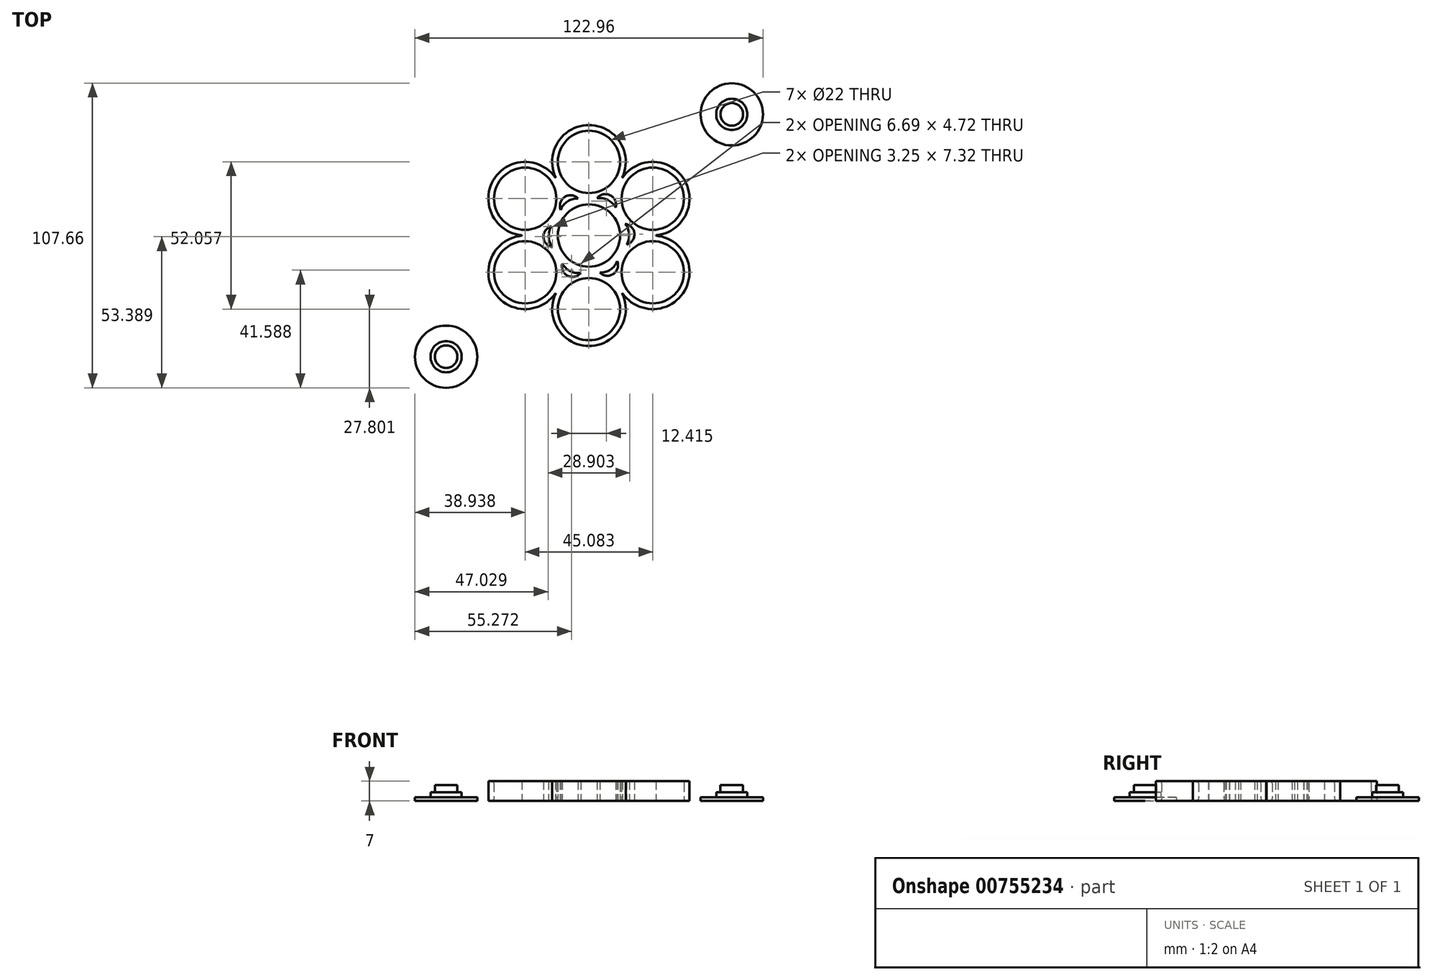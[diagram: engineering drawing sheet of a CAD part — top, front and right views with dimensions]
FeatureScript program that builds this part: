
annotation { "Feature Type Name" : "Feature", "Feature Type Description" : "" }
export const myFeature = defineFeature(function(context is Context, id is Id, definition is map)
    precondition{}
    {
        {
            var Q0;
            Q0=qCreatedBy(makeId("Top.planeOp"),FACE);
            var sketch = newSketch(context, id + "F0", { "sketchPlane" : qUnion([Q0])});
            skCircle(sketch, "E0", {"center": v(0, 0) * mm, "radius": 11 * mm});
            skCircle(sketch, "E1", {"center": v(0, 26.03) * mm, "radius": 11 * mm});
            skArc(sketch, "E2", {"start": v(11.75, 20.47) * mm, "mid": v(0, 39.03) * mm, "end": v(-11.76, 20.48) * mm});
            skCircle(sketch, "E3.1.0", {"center": v(-22.54, 13.01) * mm, "radius": 11 * mm});
            skArc(sketch, "E3.1.1", {"start": v(-11.85, 20.41) * mm, "mid": v(-33.8, 19.52) * mm, "end": v(-23.61, 0.06) * mm});
            skCircle(sketch, "E3.2.0", {"center": v(-22.54, -13.01) * mm, "radius": 11 * mm});
            skArc(sketch, "E3.2.1", {"start": v(-23.6, -0.06) * mm, "mid": v(-33.8, -19.51) * mm, "end": v(-11.86, -20.42) * mm});
            skCircle(sketch, "E3.3.0", {"center": v(0, -26.03) * mm, "radius": 11 * mm});
            skArc(sketch, "E3.3.1", {"start": v(-11.75, -20.47) * mm, "mid": v(0, -39.03) * mm, "end": v(11.76, -20.48) * mm});
            skCircle(sketch, "E3.4.0", {"center": v(22.54, -13.01) * mm, "radius": 11 * mm});
            skArc(sketch, "E3.4.1", {"start": v(11.85, -20.41) * mm, "mid": v(33.8, -19.52) * mm, "end": v(23.61, -0.06) * mm});
            skCircle(sketch, "E3.5.0", {"center": v(22.54, 13.01) * mm, "radius": 11 * mm});
            skArc(sketch, "E3.5.1", {"start": v(23.6, 0.06) * mm, "mid": v(33.8, 19.51) * mm, "end": v(11.86, 20.42) * mm});
            skArc(sketch, "E4", {"start": v(11.86, 20.42) * mm, "mid": v(11.85, 20.53) * mm, "end": v(11.75, 20.47) * mm});
            skArc(sketch, "E5.1.0", {"start": v(-11.76, 20.48) * mm, "mid": v(-11.86, 20.52) * mm, "end": v(-11.85, 20.41) * mm});
            skArc(sketch, "E5.2.0", {"start": v(-23.61, 0.06) * mm, "mid": v(-23.7, 0) * mm, "end": v(-23.6, -0.06) * mm});
            skArc(sketch, "E5.3.0", {"start": v(-11.86, -20.42) * mm, "mid": v(-11.85, -20.53) * mm, "end": v(-11.75, -20.47) * mm});
            skArc(sketch, "E5.4.0", {"start": v(11.76, -20.48) * mm, "mid": v(11.86, -20.52) * mm, "end": v(11.85, -20.41) * mm});
            skArc(sketch, "E5.5.0", {"start": v(23.61, -0.06) * mm, "mid": v(23.7, 0) * mm, "end": v(23.6, 0.06) * mm});
            skArc(sketch, "E6", {"start": v(13.27, -3.22) * mm, "mid": v(16.08, 0.62) * mm, "end": v(12.83, 4.1) * mm});
            skArc(sketch, "E7", {"start": v(13.27, -3.22) * mm, "mid": v(14.22, 0.51) * mm, "end": v(12.83, 4.1) * mm});
            skArc(sketch, "E8.1.0", {"start": v(9.42, 9.88) * mm, "mid": v(6.67, 12.57) * mm, "end": v(2.86, 13.16) * mm});
            skArc(sketch, "E8.1.1", {"start": v(9.42, 9.88) * mm, "mid": v(7.5, 14.23) * mm, "end": v(2.86, 13.16) * mm});
            skArc(sketch, "E8.2.0", {"start": v(-3.85, 13.1) * mm, "mid": v(-7.55, 12.06) * mm, "end": v(-9.97, 9.06) * mm});
            skArc(sketch, "E8.2.1", {"start": v(-3.85, 13.1) * mm, "mid": v(-8.58, 13.6) * mm, "end": v(-9.97, 9.06) * mm});
            skArc(sketch, "E8.3.0", {"start": v(-13.27, 3.22) * mm, "mid": v(-14.22, -0.51) * mm, "end": v(-12.83, -4.1) * mm});
            skArc(sketch, "E8.3.1", {"start": v(-13.27, 3.22) * mm, "mid": v(-16.08, -0.62) * mm, "end": v(-12.83, -4.1) * mm});
            skArc(sketch, "E8.4.0", {"start": v(-9.42, -9.88) * mm, "mid": v(-6.67, -12.57) * mm, "end": v(-2.86, -13.16) * mm});
            skArc(sketch, "E8.4.1", {"start": v(-9.42, -9.88) * mm, "mid": v(-7.5, -14.23) * mm, "end": v(-2.86, -13.16) * mm});
            skArc(sketch, "E8.5.0", {"start": v(3.85, -13.1) * mm, "mid": v(7.55, -12.06) * mm, "end": v(9.97, -9.06) * mm});
            skArc(sketch, "E8.5.1", {"start": v(3.85, -13.1) * mm, "mid": v(8.58, -13.6) * mm, "end": v(9.97, -9.06) * mm});
            skSolve(sketch);
        }
        {
            var Q0;
            Q0 = qSketchRegion(id + "F0", true);
            extrude(context, id + "F1", {"entities" : qUnion([Q0]), "depth" : 7 * mm, "offsetDistance" : 25 * mm});
        }
        {
            var Q0;
            Q0=qCreatedBy(makeId("Top.planeOp"),FACE);
            var sketch = newSketch(context, id + "F2", { "sketchPlane" : qUnion([Q0])});
            skCircle(sketch, "E9", {"center": v(50.48, 42.83) * mm, "radius": 11 * mm});
            skCircle(sketch, "E10.1.0", {"center": v(-50.48, -42.83) * mm, "radius": 11 * mm});
            skPoint(sketch, "E10.center", {"position": v(0, 0) * mm});
            skSolve(sketch);
        }
        {
            var Q0;
            Q0 = qSketchRegion(id + "F2", true);
            extrude(context, id + "F3", {"entities" : qUnion([Q0]), "depth" : 1.3 * mm, "offsetDistance" : 25 * mm});
        }
        {
            var Q0;
            Q0=makeQuery(id+"F3.opExtrude","CAP_FACE",FACE,{"disambiguationData":[OSD([sQuery(id+"F2.wireOp",EDGE,"E9")])],"isStart":false});
            var sketch = newSketch(context, id + "F4", { "sketchPlane" : qUnion([Q0])});
            skCircle(sketch, "E11", {"center": v(50.48, 42.83) * mm, "radius": 5.51 * mm});
            skCircle(sketch, "E12.1.0", {"center": v(-50.48, -42.83) * mm, "radius": 5.51 * mm});
            skPoint(sketch, "E12.center", {"position": v(0, 0) * mm});
            skSolve(sketch);
        }
        {
            var Q0;
            Q0 = qSketchRegion(id + "F4", true);
            extrude(context, id + "F5", {"entities" : qUnion([Q0]), "operationType" : NewBodyOperationType.ADD, "depth" : 1.74 * mm, "offsetDistance" : 25 * mm});
        }
        {
            var Q0;
            Q0=makeQuery(id+"F5.opExtrude","CAP_FACE",FACE,{"disambiguationData":[OSD([sQuery(id+"F4.wireOp",EDGE,"E11")])],"isStart":false});
            var sketch = newSketch(context, id + "F6", { "sketchPlane" : qUnion([Q0])});
            skCircle(sketch, "E13", {"center": v(50.48, 42.83) * mm, "radius": 4 * mm});
            skCircle(sketch, "E14.1.0", {"center": v(-50.48, -42.83) * mm, "radius": 4 * mm});
            skPoint(sketch, "E14.center", {"position": v(0, 0) * mm});
            skSolve(sketch);
        }
        {
            var Q0;
            Q0 = qSketchRegion(id + "F6", true);
            extrude(context, id + "F7", {"entities" : qUnion([Q0]), "operationType" : NewBodyOperationType.ADD, "depth" : 2.6 * mm, "offsetDistance" : 25 * mm});
        }
        {
            var Q0;
            Q0=makeQuery(id+"F1.opExtrude","CAP_EDGE",EDGE,{"disambiguationData":[OSD([sQuery(id+"F0.wireOp",EDGE,"E3.3.0")])],"isStart":false});
            var Q1;
            Q1=makeQuery(id+"F1.opExtrude","CAP_EDGE",EDGE,{"disambiguationData":[OSD([sQuery(id+"F0.wireOp",EDGE,"E3.4.0")])],"isStart":false});
            var Q2;
            Q2=makeQuery(id+"F1.opExtrude","CAP_EDGE",EDGE,{"disambiguationData":[OSD([sQuery(id+"F0.wireOp",EDGE,"E3.5.0")])],"isStart":false});
            var Q3;
            Q3=makeQuery(id+"F1.opExtrude","CAP_EDGE",EDGE,{"disambiguationData":[OSD([sQuery(id+"F0.wireOp",EDGE,"E1")])],"isStart":false});
            var Q4;
            Q4=makeQuery(id+"F1.opExtrude","CAP_EDGE",EDGE,{"disambiguationData":[OSD([sQuery(id+"F0.wireOp",EDGE,"E3.1.0")])],"isStart":false});
            var Q5;
            Q5=makeQuery(id+"F1.opExtrude","CAP_EDGE",EDGE,{"disambiguationData":[OSD([sQuery(id+"F0.wireOp",EDGE,"E3.2.0")])],"isStart":false});
            fillet(context, id + "F8", {"entities" : qUnion([Q0, Q1, Q2, Q3, Q4, Q5]), "radius" : 0.72 * mm, "tangentPropagation" : true, "allowEdgeOverflow" : false});
        }
        {
            var Q0;
            Q0=makeQuery(id+"F1.opExtrude","CAP_EDGE",EDGE,{"disambiguationData":[OSD([sQuery(id+"F0.wireOp",EDGE,"E3.5.0")])],"isStart":true});
            var Q1;
            Q1=makeQuery(id+"F1.opExtrude","CAP_EDGE",EDGE,{"disambiguationData":[OSD([sQuery(id+"F0.wireOp",EDGE,"E1")])],"isStart":true});
            var Q2;
            Q2=makeQuery(id+"F1.opExtrude","CAP_EDGE",EDGE,{"disambiguationData":[OSD([sQuery(id+"F0.wireOp",EDGE,"E3.1.0")])],"isStart":true});
            var Q3;
            Q3=makeQuery(id+"F1.opExtrude","CAP_EDGE",EDGE,{"disambiguationData":[OSD([sQuery(id+"F0.wireOp",EDGE,"E3.2.0")])],"isStart":true});
            var Q4;
            Q4=makeQuery(id+"F1.opExtrude","CAP_EDGE",EDGE,{"disambiguationData":[OSD([sQuery(id+"F0.wireOp",EDGE,"E3.3.0")])],"isStart":true});
            var Q5;
            Q5=makeQuery(id+"F1.opExtrude","CAP_EDGE",EDGE,{"disambiguationData":[OSD([sQuery(id+"F0.wireOp",EDGE,"E3.4.0")])],"isStart":true});
            fillet(context, id + "F9", {"entities" : qUnion([Q0, Q1, Q2, Q3, Q4, Q5]), "radius" : 1.09 * mm, "tangentPropagation" : true, "allowEdgeOverflow" : false});
        }
    });
